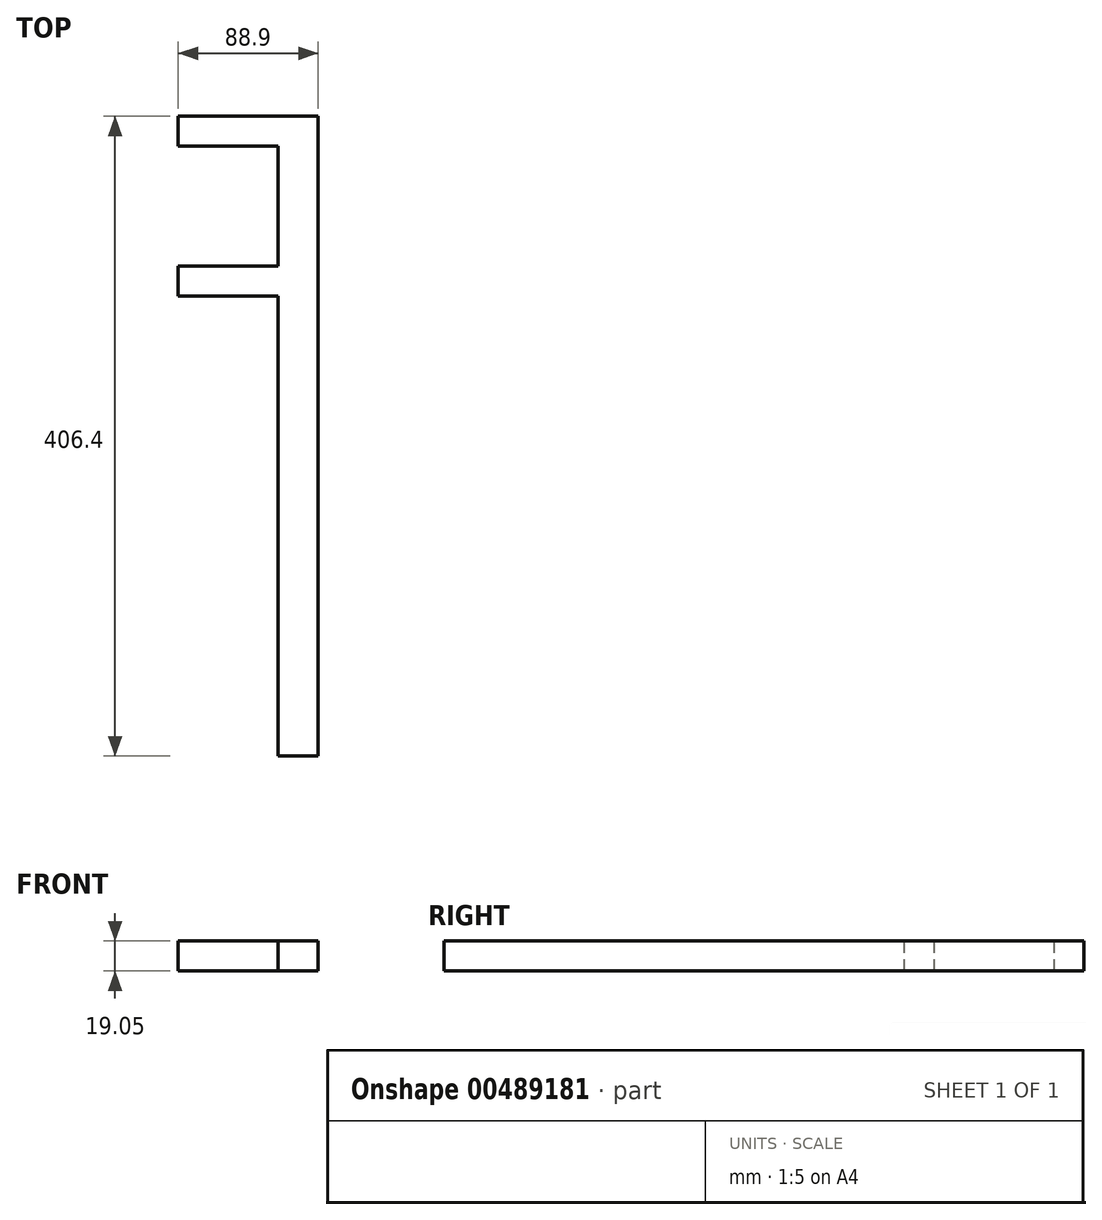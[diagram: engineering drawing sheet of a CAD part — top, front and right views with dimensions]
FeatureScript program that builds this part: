
annotation { "Feature Type Name" : "Feature", "Feature Type Description" : "" }
export const myFeature = defineFeature(function(context is Context, id is Id, definition is map)
    precondition{}
    {
        {
            var Q0;
            Q0=qCreatedBy(makeId("Top.planeOp"),FACE);
            var sketch = newSketch(context, id + "F0", { "sketchPlane" : qUnion([Q0])});
            skLineSegment(sketch, "E0", {"start": v(-35.81, -28.4) * mm, "end": v(-35.81, 378) * mm});
            skLineSegment(sketch, "E1", {"start": v(-35.81, 378) * mm, "end": v(-10.41, 378) * mm});
            skLineSegment(sketch, "E2", {"start": v(-10.41, 378) * mm, "end": v(-10.41, -28.4) * mm});
            skLineSegment(sketch, "E3", {"start": v(-35.81, -28.4) * mm, "end": v(-10.41, -28.4) * mm});
            skLineSegment(sketch, "E4", {"start": v(-35.81, 378) * mm, "end": v(-35.81, 263.7) * mm, "construction": true});
            skLineSegment(sketch, "E5", {"start": v(-75.96, 347.83) * mm, "end": v(-75.96, 293.85) * mm, "construction": true});
            skLineSegment(sketch, "E6", {"start": v(-75.96, 320.84) * mm, "end": v(-35.81, 320.84) * mm, "construction": true});
            skLineSegment(sketch, "E7", {"start": v(-35.81, 378) * mm, "end": v(-99.31, 378) * mm});
            skLineSegment(sketch, "E8", {"start": v(-35.81, 263.7) * mm, "end": v(-99.31, 263.7) * mm});
            skLineSegment(sketch, "E9", {"start": v(-99.31, 263.7) * mm, "end": v(-99.31, 282.74) * mm});
            skLineSegment(sketch, "E10", {"start": v(-99.31, 282.74) * mm, "end": v(-35.81, 282.74) * mm});
            skLineSegment(sketch, "E11", {"start": v(-99.31, 378) * mm, "end": v(-99.31, 358.94) * mm});
            skLineSegment(sketch, "E12", {"start": v(-99.31, 358.94) * mm, "end": v(-35.81, 358.94) * mm});
            skSolve(sketch);
        }
        {
            var Q0;
            Q0 = qSketchRegion(id + "F0", true);
            extrude(context, id + "F1", {"entities" : qUnion([Q0]), "depth" : 19.05 * mm, "offsetDistance" : 25.4 * mm});
        }
    });
